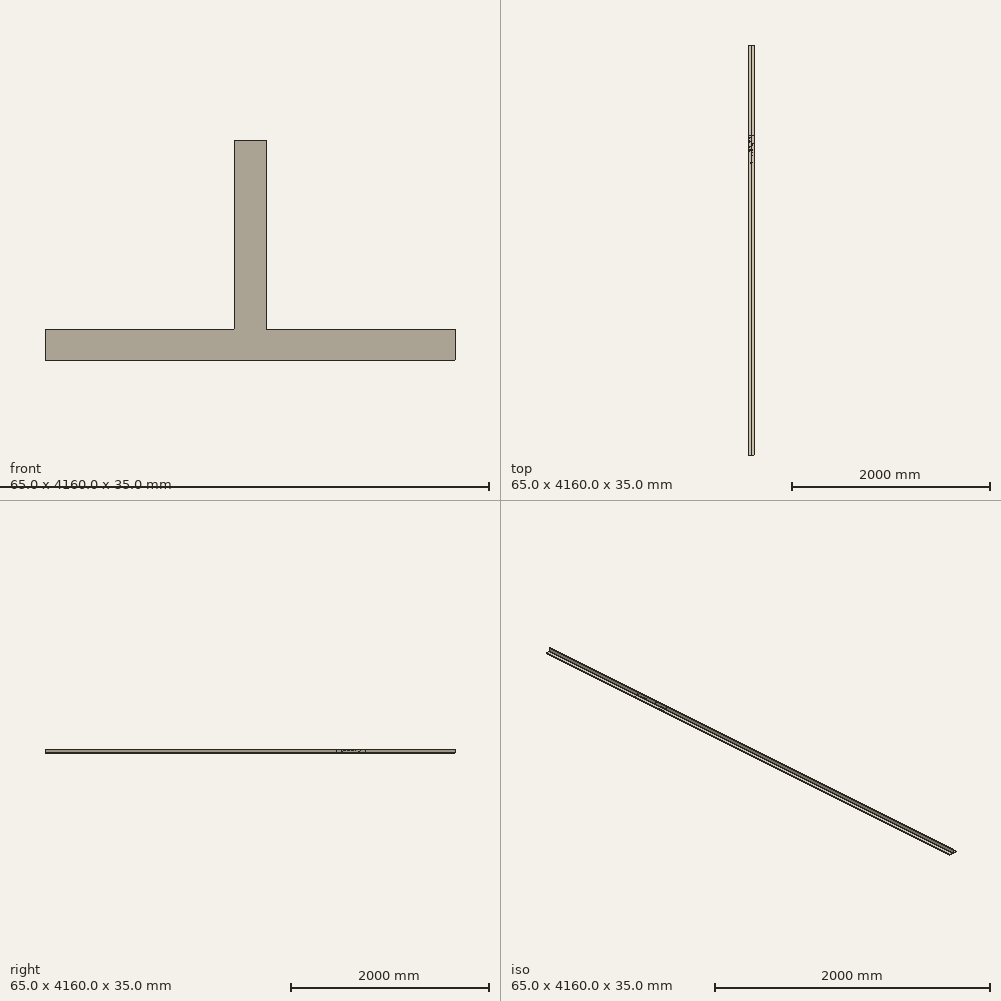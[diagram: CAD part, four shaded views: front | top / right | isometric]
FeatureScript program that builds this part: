
annotation { "Feature Type Name" : "Feature", "Feature Type Description" : "" }
export const myFeature = defineFeature(function(context is Context, id is Id, definition is map)
    precondition{}
    {
        {
            var Q0;
            Q0=qCreatedBy(makeId("Front.planeOp"),FACE);
            var sketch = newSketch(context, id + "F0", { "sketchPlane" : qUnion([Q0])});
            skLineSegment(sketch, "E0", {"start": v(-32.5, 0) * mm, "end": v(32.5, 0) * mm});
            skLineSegment(sketch, "E1", {"start": v(32.5, 0) * mm, "end": v(32.5, 5) * mm});
            skLineSegment(sketch, "E2", {"start": v(32.5, 5) * mm, "end": v(2.5, 5) * mm});
            skLineSegment(sketch, "E3", {"start": v(2.5, 5) * mm, "end": v(2.5, 35) * mm});
            skLineSegment(sketch, "E4", {"start": v(2.5, 35) * mm, "end": v(-2.5, 35) * mm});
            skLineSegment(sketch, "E5", {"start": v(-2.5, 35) * mm, "end": v(-2.5, 5) * mm});
            skLineSegment(sketch, "E6", {"start": v(-2.5, 5) * mm, "end": v(-32.5, 5) * mm});
            skLineSegment(sketch, "E7", {"start": v(-32.5, 5) * mm, "end": v(-32.5, 0) * mm});
            skLineSegment(sketch, "E8", {"start": v(0, 35) * mm, "end": v(0, 0) * mm, "construction": true});
            skSolve(sketch);
        }
        {
            var Q0;
            Q0=makeQuery(id+"F0.imprint","IMPRINT",FACE,{"disambiguationData":[TD([[makeQuery(id+"F0.imprint","IMPRINT",EDGE,{"derivedFrom":sQuery(id+"F0.wireOp",EDGE,"E0")}),1.0]])]});
            extrude(context, id + "F1", {"entities" : qUnion([Q0]), "depth" : 300 * mm});
        }
        {
            var Q0;
            Q0=makeQuery(id+"F0.imprint","IMPRINT",FACE,{"disambiguationData":[TD([[makeQuery(id+"F0.imprint","IMPRINT",EDGE,{"derivedFrom":sQuery(id+"F0.wireOp",EDGE,"E0")}),1.0]])]});
            extrude(context, id + "F2", {"entities" : qUnion([Q0]), "depth" : 3250 * mm});
        }
        {
            var Q0;
            Q0=qSketchRegion(id+"F0",true);
            extrude(context, id + "F3", {"entities" : qUnion([Q0]), "oppositeDirection" : true, "depth" : 910 * mm});
        }
    });
